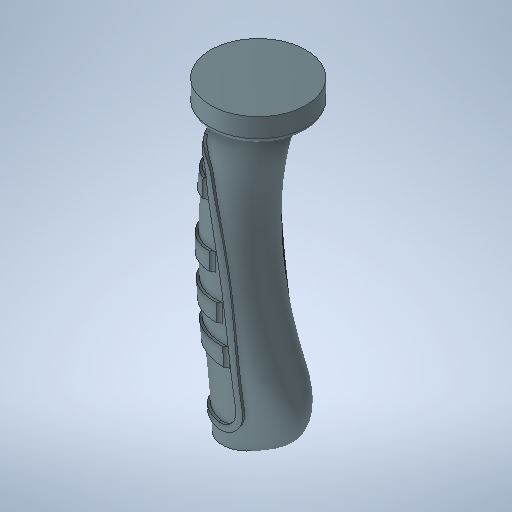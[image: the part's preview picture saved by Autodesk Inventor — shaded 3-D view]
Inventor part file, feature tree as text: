
AUTODESK INVENTOR PART (.ipt)
format: ipt  version: 2025.1 (Build 291241000, 241)  size: 3,545,600 bytes
history: native  units: mm
features: other x18, sketch x7, plane x3, fillet x3, loft x1, shell x1, extrude x1, projected_geometry x1
ambient origin geometry x8: Origin, YZ Plane, XZ Plane, XY Plane, X Axis, Y Axis, Z Axis, Center Point
bodies: Volumenkörper1 (feature_tree)
feature tree (35):
  sketch  "Skizze2"  dims[d2=240.0mm d3=550.0mm d4=210.0mm]
  other  "Arbeitspunkt1"
  plane  "Arbeitsebene1"
  sketch  "Skizze3"  dims[d5=40.0mm d6=12.0mm d7=240.0mm d8=240.0mm d9=52.0mm]
  other  "Arbeitspunkt2"
  other  "Arbeitspunkt3"
  plane  "Arbeitsebene2"
  loft  "Erhebung1"
  shell  "Wandung1"  Thickness=210.0mm
  extrude  "Extrusion1"  Depth=12.0mm
  fillet  "Rundung1"  Radius=240.0mm
  fillet  "Rundung2"  Radius=240.0mm
  plane  "Arbeitsebene3"
  sketch  "Skizze6"  dims[d12=42.0mm]
  other  "3D-Skizze1"
  sketch  "3D Sketch4"
  other  "Trennen3"
  other  "Trennen4"
  other  "Verdickung2"
  sketch  "Skizze7"  dims[d13=0.0mm d14=90.0deg d15=0.0mm d16=90.0deg d17=0.0mm d18=90.0deg d19=0.0mm d20=90.0deg d21=2.0mm d22=80.0mm d23=20.0mm d24=0.0mm d25=2.0mm d26=4.0mm d27=26.0mm d28=2.0mm d29=5.0mm d30=20.0mm d31=22.0mm d32=12.0mm d34=45.0mm d35=160.0mm d36=28.0mm d37=23.045016mm d38=552.0mm d41=2.0mm d42=2.0mm d43=2.0mm d44=15.0mm d45=15.0mm d46=15.0mm d47=15.0mm d52=20.0mm d53=60.0mm d54=90.0mm d55=125.0mm d56=70.0mm d57=5.0mm d58=5.0mm d59=5.0mm d60=2.0mm d61=2.0mm d62=2.0mm d63=2.0mm d64=2.0mm d65=2.0mm d66=2.0mm d67=2.0mm d68=2.0mm d69=2.0mm d70=2.0mm d71=2.0mm d72=4.0mm]
  other  "3D-Skizze3"
  other  "Trennen6"
  other  "Trennen7"
  other  "Trennen8"
  other  "Trennen9"
  other  "Verdickung3"
  other  "Verdickung4"
  other  "Verdickung5"
  other  "Verdickung6"
  fillet  "Rundung3"  Radius=52.0mm
  sketch  "Skizze4"  dims[d10=42.0mm]
  sketch  "Skizze5"  dims[d11=52.0mm]
  other  "Auf Fläche projizieren1"
  projected_geometry  "Projizierte Kontur1"
  other  "Auf Fläche projizieren2"
